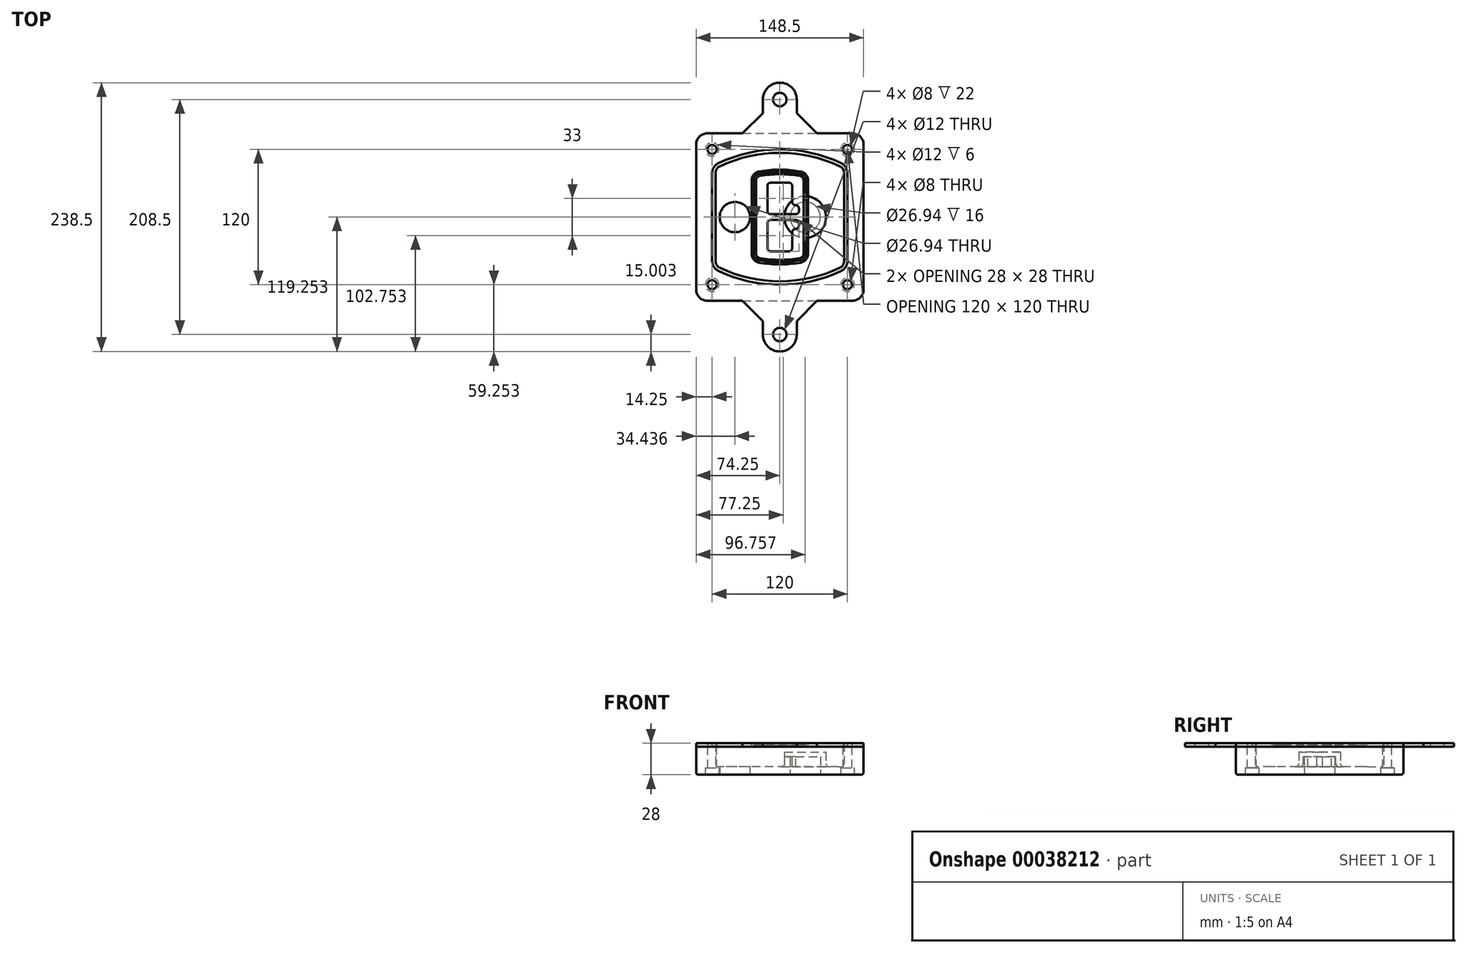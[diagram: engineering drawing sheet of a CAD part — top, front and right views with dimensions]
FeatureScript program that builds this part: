
annotation { "Feature Type Name" : "Feature", "Feature Type Description" : "" }
export const myFeature = defineFeature(function(context is Context, id is Id, definition is map)
    precondition{}
    {
        {
            var Q0;
            Q0=qCreatedBy(makeId("Top.planeOp"),FACE);
            var sketch = newSketch(context, id + "F0", { "sketchPlane" : qUnion([Q0])});
            skPoint(sketch, "E0.rect.middle", {"position": v(0, 0) * mm});
            skLineSegment(sketch, "E1.bottom", {"start": v(24.05, 28.38) * mm, "end": v(152.55, 28.38) * mm});
            skLineSegment(sketch, "E1.top", {"start": v(24.05, 176.88) * mm, "end": v(152.55, 176.88) * mm});
            skLineSegment(sketch, "E1.left", {"start": v(14.05, 38.38) * mm, "end": v(14.05, 166.88) * mm});
            skLineSegment(sketch, "E1.right", {"start": v(162.55, 38.38) * mm, "end": v(162.55, 166.88) * mm});
            skLineSegment(sketch, "E2", {"start": v(14.05, 176.88) * mm, "end": v(162.55, 28.38) * mm, "construction": true});
            skLineSegment(sketch, "E3", {"start": v(162.55, 176.88) * mm, "end": v(14.05, 28.38) * mm, "construction": true});
            skCircle(sketch, "E4", {"center": v(28.3, 162.63) * mm, "radius": 4 * mm});
            skCircle(sketch, "E5", {"center": v(148.3, 162.63) * mm, "radius": 4 * mm});
            skCircle(sketch, "E6", {"center": v(148.3, 42.63) * mm, "radius": 4 * mm});
            skCircle(sketch, "E7", {"center": v(28.3, 42.63) * mm, "radius": 4 * mm});
            skLineSegment(sketch, "E8", {"start": v(28.3, 162.63) * mm, "end": v(148.3, 162.63) * mm, "construction": true});
            skLineSegment(sketch, "E9", {"start": v(148.3, 162.63) * mm, "end": v(148.3, 42.63) * mm, "construction": true});
            skLineSegment(sketch, "E10", {"start": v(148.3, 42.63) * mm, "end": v(28.3, 42.63) * mm, "construction": true});
            skLineSegment(sketch, "E11", {"start": v(28.3, 42.63) * mm, "end": v(28.3, 162.63) * mm, "construction": true});
            skLineSegment(sketch, "E12", {"start": v(28.3, 141.46) * mm, "end": v(28.3, 63.8) * mm});
            skLineSegment(sketch, "E13", {"start": v(148.3, 141.46) * mm, "end": v(148.3, 63.8) * mm});
            skArc(sketch, "E14", {"start": v(142.56, 150.51) * mm, "mid": v(88.3, 162.63) * mm, "end": v(34.04, 150.51) * mm});
            skArc(sketch, "E15", {"start": v(34.04, 54.75) * mm, "mid": v(88.3, 42.63) * mm, "end": v(142.56, 54.75) * mm});
            skLineSegment(sketch, "E16", {"start": v(28.3, 102.63) * mm, "end": v(148.3, 102.63) * mm, "construction": true});
            skPoint(sketch, "E17.visualSharp", {"position": v(28.3, 57.63) * mm});
            skArc(sketch, "E17.filletArc", {"start": v(28.3, 63.8) * mm, "mid": v(29.86, 58.44) * mm, "end": v(34.04, 54.75) * mm});
            skPoint(sketch, "E18.visualSharp", {"position": v(28.3, 147.63) * mm});
            skArc(sketch, "E18.filletArc", {"start": v(34.04, 150.51) * mm, "mid": v(29.86, 146.82) * mm, "end": v(28.3, 141.46) * mm});
            skPoint(sketch, "E19.visualSharp", {"position": v(148.3, 147.63) * mm});
            skArc(sketch, "E19.filletArc", {"start": v(148.3, 141.46) * mm, "mid": v(146.74, 146.82) * mm, "end": v(142.56, 150.51) * mm});
            skPoint(sketch, "E20.visualSharp", {"position": v(148.3, 57.63) * mm});
            skArc(sketch, "E20.filletArc", {"start": v(142.56, 54.75) * mm, "mid": v(146.74, 58.44) * mm, "end": v(148.3, 63.8) * mm});
            skPoint(sketch, "E21.visualSharp", {"position": v(14.05, 176.88) * mm});
            skArc(sketch, "E21.filletArc", {"start": v(24.05, 176.88) * mm, "mid": v(16.98, 173.95) * mm, "end": v(14.05, 166.88) * mm});
            skPoint(sketch, "E22.visualSharp", {"position": v(162.55, 176.88) * mm});
            skArc(sketch, "E22.filletArc", {"start": v(162.55, 166.88) * mm, "mid": v(159.62, 173.95) * mm, "end": v(152.55, 176.88) * mm});
            skPoint(sketch, "E23.visualSharp", {"position": v(162.55, 28.38) * mm});
            skArc(sketch, "E23.filletArc", {"start": v(152.55, 28.38) * mm, "mid": v(159.62, 31.31) * mm, "end": v(162.55, 38.38) * mm});
            skPoint(sketch, "E24.visualSharp", {"position": v(14.05, 28.38) * mm});
            skArc(sketch, "E24.filletArc", {"start": v(14.05, 38.38) * mm, "mid": v(16.98, 31.31) * mm, "end": v(24.05, 28.38) * mm});
            skArc(sketch, "E25.0", {"start": v(145.3, 141.46) * mm, "mid": v(144.2, 145.22) * mm, "end": v(141.28, 147.8) * mm});
            skLineSegment(sketch, "E25.1", {"start": v(145.3, 141.46) * mm, "end": v(145.3, 63.8) * mm});
            skArc(sketch, "E25.2", {"start": v(141.28, 57.47) * mm, "mid": v(144.2, 60.05) * mm, "end": v(145.3, 63.8) * mm});
            skArc(sketch, "E25.3", {"start": v(35.32, 57.47) * mm, "mid": v(88.3, 45.63) * mm, "end": v(141.28, 57.47) * mm});
            skArc(sketch, "E25.4", {"start": v(31.3, 63.8) * mm, "mid": v(32.4, 60.05) * mm, "end": v(35.32, 57.47) * mm});
            skArc(sketch, "E25.5", {"start": v(141.28, 147.8) * mm, "mid": v(88.3, 159.63) * mm, "end": v(35.32, 147.8) * mm});
            skLineSegment(sketch, "E25.6", {"start": v(31.3, 141.46) * mm, "end": v(31.3, 63.8) * mm});
            skArc(sketch, "E25.7", {"start": v(35.32, 147.8) * mm, "mid": v(32.4, 145.22) * mm, "end": v(31.3, 141.46) * mm});
            skArc(sketch, "E26.0", {"start": v(32.34, 154.13) * mm, "mid": v(26.48, 148.97) * mm, "end": v(24.3, 141.46) * mm});
            skArc(sketch, "E26.1", {"start": v(144.26, 154.13) * mm, "mid": v(88.3, 166.63) * mm, "end": v(32.34, 154.13) * mm});
            skArc(sketch, "E26.2", {"start": v(152.3, 141.46) * mm, "mid": v(150.12, 148.97) * mm, "end": v(144.26, 154.13) * mm});
            skLineSegment(sketch, "E26.3", {"start": v(152.3, 141.46) * mm, "end": v(152.3, 63.8) * mm});
            skArc(sketch, "E26.4", {"start": v(144.26, 51.13) * mm, "mid": v(150.12, 56.3) * mm, "end": v(152.3, 63.8) * mm});
            skLineSegment(sketch, "E26.5", {"start": v(24.3, 141.46) * mm, "end": v(24.3, 63.8) * mm});
            skArc(sketch, "E26.6", {"start": v(32.34, 51.13) * mm, "mid": v(88.3, 38.63) * mm, "end": v(144.26, 51.13) * mm});
            skArc(sketch, "E26.7", {"start": v(24.3, 63.8) * mm, "mid": v(26.48, 56.3) * mm, "end": v(32.34, 51.13) * mm});
            skSolve(sketch);
        }
        {
            var Q0;
            Q0=makeQuery(id+"F0.imprint","IMPRINT",FACE,{"disambiguationData":[TD([[makeQuery(id+"F0.imprint","IMPRINT",EDGE,{"derivedFrom":sQuery(id+"F0.wireOp",EDGE,"E1.bottom")}),1.0]])]});
            var Q1;
            Q1=makeQuery(id+"F0.imprint","IMPRINT",FACE,{"disambiguationData":[TD([[makeQuery(id+"F0.imprint","IMPRINT",EDGE,{"derivedFrom":sQuery(id+"F0.wireOp",EDGE,"E12")}),1.0]])]});
            var Q2;
            Q2=makeQuery(id+"F0.imprint","IMPRINT",FACE,{"disambiguationData":[TD([[makeQuery(id+"F0.imprint","IMPRINT",EDGE,{"derivedFrom":sQuery(id+"F0.wireOp",EDGE,"E25.0")}),1.0]])]});
            var Q3;
            Q3=makeQuery(id+"F0.imprint","IMPRINT",FACE,{"disambiguationData":[TD([[makeQuery(id+"F0.imprint","IMPRINT",EDGE,{"derivedFrom":sQuery(id+"F0.wireOp",EDGE,"E12")}),-1.0]])]});
            extrude(context, id + "F1", {"entities" : qUnion([Q0, Q1, Q2, Q3]), "oppositeDirection" : true, "depth" : 25 * mm});
        }
        {
            var Q0;
            Q0=makeQuery(id+"F0.imprint","IMPRINT",FACE,{"disambiguationData":[TD([[makeQuery(id+"F0.imprint","IMPRINT",EDGE,{"derivedFrom":sQuery(id+"F0.wireOp",EDGE,"E12")}),1.0]])]});
            extrude(context, id + "F2", {"entities" : qUnion([Q0]), "operationType" : NewBodyOperationType.ADD, "depth" : 3 * mm});
        }
        {
            var Q0;
            Q0=makeQuery(id+"F0.imprint","IMPRINT",FACE,{"disambiguationData":[TD([[makeQuery(id+"F0.imprint","IMPRINT",EDGE,{"derivedFrom":sQuery(id+"F0.wireOp",EDGE,"E25.0")}),1.0]])]});
            extrude(context, id + "F3", {"entities" : qUnion([Q0]), "operationType" : NewBodyOperationType.REMOVE, "oppositeDirection" : true, "depth" : 18 * mm});
        }
        {
            var Q0;
            Q0=makeQuery(id+"F2.opExtrude","CAP_FACE",FACE,{"disambiguationData":[OSD([sQuery(id+"F0.wireOp",EDGE,"E12"),sQuery(id+"F0.wireOp",EDGE,"E13"),sQuery(id+"F0.wireOp",EDGE,"E14"),sQuery(id+"F0.wireOp",EDGE,"E15"),sQuery(id+"F0.wireOp",EDGE,"E17.filletArc"),sQuery(id+"F0.wireOp",EDGE,"E18.filletArc"),sQuery(id+"F0.wireOp",EDGE,"E19.filletArc"),sQuery(id+"F0.wireOp",EDGE,"E20.filletArc"),sQuery(id+"F0.wireOp",EDGE,"E25.0"),sQuery(id+"F0.wireOp",EDGE,"E25.1"),sQuery(id+"F0.wireOp",EDGE,"E25.2"),sQuery(id+"F0.wireOp",EDGE,"E25.3"),sQuery(id+"F0.wireOp",EDGE,"E25.4"),sQuery(id+"F0.wireOp",EDGE,"E25.5"),sQuery(id+"F0.wireOp",EDGE,"E25.6"),sQuery(id+"F0.wireOp",EDGE,"E25.7")])],"isStart":false});
            var sketch = newSketch(context, id + "F4", { "sketchPlane" : qUnion([Q0])});
            skArc(sketch, "E27.0", {"start": v(69.96, 62.18) * mm, "mid": v(88.3, 60.63) * mm, "end": v(106.64, 62.18) * mm});
            skArc(sketch, "E28.0", {"start": v(106.64, 143.09) * mm, "mid": v(88.3, 144.63) * mm, "end": v(69.96, 143.09) * mm});
            skLineSegment(sketch, "E29", {"start": v(63.3, 135.2) * mm, "end": v(63.3, 70.07) * mm});
            skLineSegment(sketch, "E30", {"start": v(113.3, 135.2) * mm, "end": v(113.3, 70.07) * mm});
            skLineSegment(sketch, "E31", {"start": v(63.3, 141.74) * mm, "end": v(113.3, 141.74) * mm, "construction": true});
            skLineSegment(sketch, "E32", {"start": v(63.3, 63.52) * mm, "end": v(113.3, 63.52) * mm, "construction": true});
            skPoint(sketch, "E33.visualSharp", {"position": v(63.3, 141.74) * mm});
            skArc(sketch, "E33.filletArc", {"start": v(69.96, 143.09) * mm, "mid": v(65.19, 140.36) * mm, "end": v(63.3, 135.2) * mm});
            skPoint(sketch, "E34.visualSharp", {"position": v(113.3, 141.74) * mm});
            skArc(sketch, "E34.filletArc", {"start": v(113.3, 135.2) * mm, "mid": v(111.41, 140.36) * mm, "end": v(106.64, 143.09) * mm});
            skPoint(sketch, "E35.visualSharp", {"position": v(113.3, 63.52) * mm});
            skArc(sketch, "E35.filletArc", {"start": v(106.64, 62.18) * mm, "mid": v(111.41, 64.9) * mm, "end": v(113.3, 70.07) * mm});
            skPoint(sketch, "E36.visualSharp", {"position": v(63.3, 63.52) * mm});
            skArc(sketch, "E36.filletArc", {"start": v(63.3, 70.07) * mm, "mid": v(65.19, 64.9) * mm, "end": v(69.96, 62.18) * mm});
            skArc(sketch, "E37.0", {"start": v(141.28, 147.8) * mm, "mid": v(88.3, 159.63) * mm, "end": v(35.32, 147.8) * mm});
            skArc(sketch, "E37.1", {"start": v(35.32, 147.8) * mm, "mid": v(32.4, 145.22) * mm, "end": v(31.3, 141.46) * mm});
            skLineSegment(sketch, "E37.2", {"start": v(31.3, 141.46) * mm, "end": v(31.3, 63.8) * mm});
            skArc(sketch, "E37.3", {"start": v(31.3, 63.8) * mm, "mid": v(32.4, 60.05) * mm, "end": v(35.32, 57.47) * mm});
            skArc(sketch, "E37.4", {"start": v(35.32, 57.47) * mm, "mid": v(88.3, 45.63) * mm, "end": v(141.28, 57.47) * mm});
            skArc(sketch, "E37.5", {"start": v(141.28, 57.47) * mm, "mid": v(144.2, 60.05) * mm, "end": v(145.3, 63.8) * mm});
            skLineSegment(sketch, "E37.6", {"start": v(145.3, 141.46) * mm, "end": v(145.3, 63.8) * mm});
            skArc(sketch, "E37.7", {"start": v(145.3, 141.46) * mm, "mid": v(144.2, 145.22) * mm, "end": v(141.28, 147.8) * mm});
            skLineSegment(sketch, "E38.0", {"start": v(111.3, 135.2) * mm, "end": v(111.3, 70.07) * mm});
            skArc(sketch, "E38.1", {"start": v(106.3, 64.15) * mm, "mid": v(109.88, 66.2) * mm, "end": v(111.3, 70.07) * mm});
            skArc(sketch, "E38.2", {"start": v(70.3, 64.15) * mm, "mid": v(88.3, 62.63) * mm, "end": v(106.3, 64.15) * mm});
            skArc(sketch, "E38.3", {"start": v(65.3, 70.07) * mm, "mid": v(66.72, 66.2) * mm, "end": v(70.3, 64.15) * mm});
            skLineSegment(sketch, "E38.4", {"start": v(65.3, 135.2) * mm, "end": v(65.3, 70.07) * mm});
            skArc(sketch, "E38.5", {"start": v(111.3, 135.2) * mm, "mid": v(109.88, 139.07) * mm, "end": v(106.3, 141.11) * mm});
            skArc(sketch, "E38.6", {"start": v(70.3, 141.11) * mm, "mid": v(66.72, 139.07) * mm, "end": v(65.3, 135.2) * mm});
            skArc(sketch, "E38.7", {"start": v(106.3, 141.11) * mm, "mid": v(88.3, 142.63) * mm, "end": v(70.3, 141.11) * mm});
            skArc(sketch, "E39.0", {"start": v(109.3, 135.2) * mm, "mid": v(108.36, 137.78) * mm, "end": v(105.97, 139.14) * mm});
            skLineSegment(sketch, "E39.1", {"start": v(109.3, 135.2) * mm, "end": v(109.3, 70.07) * mm});
            skArc(sketch, "E39.2", {"start": v(105.97, 66.12) * mm, "mid": v(108.36, 67.49) * mm, "end": v(109.3, 70.07) * mm});
            skArc(sketch, "E39.3", {"start": v(70.63, 66.12) * mm, "mid": v(88.3, 64.63) * mm, "end": v(105.97, 66.12) * mm});
            skArc(sketch, "E39.4", {"start": v(67.3, 70.07) * mm, "mid": v(68.24, 67.49) * mm, "end": v(70.63, 66.12) * mm});
            skArc(sketch, "E39.5", {"start": v(105.97, 139.14) * mm, "mid": v(88.3, 140.63) * mm, "end": v(70.63, 139.14) * mm});
            skLineSegment(sketch, "E39.6", {"start": v(67.3, 135.2) * mm, "end": v(67.3, 70.07) * mm});
            skArc(sketch, "E39.7", {"start": v(70.63, 139.14) * mm, "mid": v(68.24, 137.78) * mm, "end": v(67.3, 135.2) * mm});
            skLineSegment(sketch, "E40", {"start": v(63.3, 102.63) * mm, "end": v(113.3, 102.63) * mm, "construction": true});
            skLineSegment(sketch, "E41", {"start": v(77.3, 108.13) * mm, "end": v(77.3, 130.13) * mm});
            skLineSegment(sketch, "E42", {"start": v(80.3, 133.13) * mm, "end": v(96.3, 133.13) * mm});
            skLineSegment(sketch, "E43", {"start": v(99.3, 130.13) * mm, "end": v(99.3, 116.13) * mm});
            skLineSegment(sketch, "E44", {"start": v(102.3, 113.13) * mm, "end": v(102.3, 113.13) * mm});
            skLineSegment(sketch, "E45", {"start": v(105.3, 110.13) * mm, "end": v(105.3, 108.13) * mm});
            skLineSegment(sketch, "E46", {"start": v(102.3, 105.13) * mm, "end": v(80.3, 105.13) * mm});
            skPoint(sketch, "E47.visualSharp", {"position": v(77.3, 133.13) * mm});
            skArc(sketch, "E47.filletArc", {"start": v(80.3, 133.13) * mm, "mid": v(78.18, 132.25) * mm, "end": v(77.3, 130.13) * mm});
            skPoint(sketch, "E48.visualSharp", {"position": v(99.3, 133.13) * mm});
            skArc(sketch, "E48.filletArc", {"start": v(99.3, 130.13) * mm, "mid": v(98.42, 132.25) * mm, "end": v(96.3, 133.13) * mm});
            skPoint(sketch, "E49.visualSharp", {"position": v(99.3, 113.13) * mm});
            skArc(sketch, "E49.filletArc", {"start": v(99.3, 116.13) * mm, "mid": v(100.18, 114.01) * mm, "end": v(102.3, 113.13) * mm});
            skPoint(sketch, "E50.visualSharp", {"position": v(105.3, 113.13) * mm});
            skArc(sketch, "E50.filletArc", {"start": v(105.3, 110.13) * mm, "mid": v(104.42, 112.25) * mm, "end": v(102.3, 113.13) * mm});
            skPoint(sketch, "E51.visualSharp", {"position": v(105.3, 105.13) * mm});
            skArc(sketch, "E51.filletArc", {"start": v(102.3, 105.13) * mm, "mid": v(104.42, 106.01) * mm, "end": v(105.3, 108.13) * mm});
            skPoint(sketch, "E52.visualSharp", {"position": v(77.3, 105.13) * mm});
            skArc(sketch, "E52.filletArc", {"start": v(77.3, 108.13) * mm, "mid": v(78.18, 106.01) * mm, "end": v(80.3, 105.13) * mm});
            skLineSegment(sketch, "E53.0.MirrorCS", {"start": v(102.3, 100.13) * mm, "end": v(80.3, 100.13) * mm});
            skArc(sketch, "E54.0.MirrorCS", {"start": v(77.3, 97.13) * mm, "mid": v(78.18, 99.25) * mm, "end": v(80.3, 100.13) * mm});
            skLineSegment(sketch, "E55.0.MirrorCS", {"start": v(77.3, 97.13) * mm, "end": v(77.3, 75.13) * mm});
            skArc(sketch, "E56.0.MirrorCS", {"start": v(80.3, 72.13) * mm, "mid": v(78.18, 73.01) * mm, "end": v(77.3, 75.13) * mm});
            skLineSegment(sketch, "E57.0.MirrorCS", {"start": v(80.3, 72.13) * mm, "end": v(96.3, 72.13) * mm});
            skArc(sketch, "E58.0.MirrorCS", {"start": v(99.3, 75.13) * mm, "mid": v(98.42, 73.01) * mm, "end": v(96.3, 72.13) * mm});
            skLineSegment(sketch, "E59.0.MirrorCS", {"start": v(99.3, 75.13) * mm, "end": v(99.3, 89.13) * mm});
            skArc(sketch, "E60.0.MirrorCS", {"start": v(99.3, 89.13) * mm, "mid": v(100.18, 91.25) * mm, "end": v(102.3, 92.13) * mm});
            skArc(sketch, "E61.0.MirrorCS", {"start": v(105.3, 95.13) * mm, "mid": v(104.42, 93.01) * mm, "end": v(102.3, 92.13) * mm});
            skLineSegment(sketch, "E62.0.MirrorCS", {"start": v(105.3, 95.13) * mm, "end": v(105.3, 97.13) * mm});
            skArc(sketch, "E63.0.MirrorCS", {"start": v(102.3, 100.13) * mm, "mid": v(104.42, 99.25) * mm, "end": v(105.3, 97.13) * mm});
            skSolve(sketch);
        }
        {
            var Q0;
            Q0=makeQuery(id+"F4.imprint","IMPRINT",FACE,{"disambiguationData":[TD([[makeQuery(id+"F4.imprint","IMPRINT",EDGE,{"derivedFrom":sQuery(id+"F4.wireOp",EDGE,"E27.0")}),1.0]])]});
            var Q1;
            Q1=makeQuery(id+"F4.imprint","IMPRINT",FACE,{"disambiguationData":[TD([[makeQuery(id+"F4.imprint","IMPRINT",EDGE,{"derivedFrom":sQuery(id+"F4.wireOp",EDGE,"E38.0")}),-1.0]])]});
            var Q2;
            Q2=makeQuery(id+"F4.imprint","IMPRINT",FACE,{"disambiguationData":[TD([[makeQuery(id+"F4.imprint","IMPRINT",EDGE,{"derivedFrom":sQuery(id+"F4.wireOp",EDGE,"E39.0")}),1.0]])]});
            extrude(context, id + "F5", {"entities" : qUnion([Q0, Q1, Q2]), "operationType" : NewBodyOperationType.ADD, "endBound" : BoundingType.UP_TO_NEXT, "oppositeDirection" : true, "depth" : 25 * mm});
        }
        {
            var Q0;
            Q0=makeQuery(id+"F4.imprint","IMPRINT",FACE,{"disambiguationData":[TD([[makeQuery(id+"F4.imprint","IMPRINT",EDGE,{"derivedFrom":sQuery(id+"F4.wireOp",EDGE,"E38.0")}),-1.0]])]});
            extrude(context, id + "F6", {"entities" : qUnion([Q0]), "operationType" : NewBodyOperationType.REMOVE, "oppositeDirection" : true, "depth" : 2 * mm});
        }
        {
            var Q0;
            Q0=makeQuery(id+"F1.opExtrude","CAP_FACE",FACE,{"disambiguationData":[OSD([sQuery(id+"F0.wireOp",EDGE,"E1.bottom"),sQuery(id+"F0.wireOp",EDGE,"E1.top"),sQuery(id+"F0.wireOp",EDGE,"E1.left"),sQuery(id+"F0.wireOp",EDGE,"E1.right"),sQuery(id+"F0.wireOp",EDGE,"E4"),sQuery(id+"F0.wireOp",EDGE,"E5"),sQuery(id+"F0.wireOp",EDGE,"E6"),sQuery(id+"F0.wireOp",EDGE,"E7"),sQuery(id+"F0.wireOp",EDGE,"E21.filletArc"),sQuery(id+"F0.wireOp",EDGE,"E22.filletArc"),sQuery(id+"F0.wireOp",EDGE,"E23.filletArc"),sQuery(id+"F0.wireOp",EDGE,"E24.filletArc")])],"isStart":false});
            var sketch = newSketch(context, id + "F7", { "sketchPlane" : qUnion([Q0])});
            skCircle(sketch, "E64", {"center": v(110.8, -102.63) * mm, "radius": 13.47 * mm});
            skCircle(sketch, "E65", {"center": v(48.49, -102.63) * mm, "radius": 13.47 * mm});
            skLineSegment(sketch, "E66", {"start": v(162.55, -102.63) * mm, "end": v(14.05, -102.63) * mm});
            skCircle(sketch, "E67", {"center": v(110.8, -102.63) * mm, "radius": 18.47 * mm});
            skCircle(sketch, "E68", {"center": v(148.3, -162.63) * mm, "radius": 6 * mm});
            skCircle(sketch, "E69", {"center": v(28.3, -162.63) * mm, "radius": 6 * mm});
            skCircle(sketch, "E70", {"center": v(28.3, -42.63) * mm, "radius": 6 * mm});
            skCircle(sketch, "E71", {"center": v(148.3, -42.63) * mm, "radius": 6 * mm});
            skSolve(sketch);
        }
        {
            var Q0;
            {var subQ1=sQuery(id+"F7.wireOp",EDGE,"E66");var subQ4=sQuery(id+"F7.wireOp",EDGE,"E64");var subQ6=makeQuery(id+"F7.imprint","INTERSECT",VERTEX,{"disambiguationData":[OD(0.0)],"derivedFrom":[subQ4,subQ1]});Q0=makeQuery(id+"F7.imprint","IMPRINT",FACE,{"disambiguationData":[TD([[makeQuery(id+"F7.imprint","IMPRINT",EDGE,{"disambiguationData":[TD([[subQ6,-1.0]])],"derivedFrom":subQ4}),-1.0]])]});}
            var Q1;
            {var subQ0=sQuery(id+"F7.wireOp",EDGE,"E66");var subQ1=sQuery(id+"F7.wireOp",EDGE,"E64");var subQ3=makeQuery(id+"F7.imprint","INTERSECT",VERTEX,{"disambiguationData":[OD(0.0)],"derivedFrom":[subQ1,subQ0]});Q1=makeQuery(id+"F7.imprint","IMPRINT",FACE,{"disambiguationData":[TD([[makeQuery(id+"F7.imprint","IMPRINT",EDGE,{"disambiguationData":[TD([[subQ3,-1.0]])],"derivedFrom":subQ1}),1.0]])]});}
            var Q2;
            {var subQ0=sQuery(id+"F7.wireOp",EDGE,"E66");var subQ1=sQuery(id+"F7.wireOp",EDGE,"E64");var subQ3=makeQuery(id+"F7.imprint","INTERSECT",VERTEX,{"disambiguationData":[OD(0.0)],"derivedFrom":[subQ1,subQ0]});Q2=makeQuery(id+"F7.imprint","IMPRINT",FACE,{"disambiguationData":[TD([[makeQuery(id+"F7.imprint","IMPRINT",EDGE,{"disambiguationData":[TD([[subQ3,1.0]])],"derivedFrom":subQ1}),1.0]])]});}
            var Q3;
            {var subQ1=sQuery(id+"F7.wireOp",EDGE,"E66");var subQ4=sQuery(id+"F7.wireOp",EDGE,"E64");var subQ6=makeQuery(id+"F7.imprint","INTERSECT",VERTEX,{"disambiguationData":[OD(0.0)],"derivedFrom":[subQ4,subQ1]});Q3=makeQuery(id+"F7.imprint","IMPRINT",FACE,{"disambiguationData":[TD([[makeQuery(id+"F7.imprint","IMPRINT",EDGE,{"disambiguationData":[TD([[subQ6,1.0]])],"derivedFrom":subQ4}),-1.0]])]});}
            extrude(context, id + "F8", {"entities" : qUnion([Q0, Q1, Q2, Q3]), "operationType" : NewBodyOperationType.ADD, "oppositeDirection" : true, "depth" : 20 * mm});
        }
        {
            var Q0;
            {var subQ0=sQuery(id+"F7.wireOp",EDGE,"E66");var subQ1=sQuery(id+"F7.wireOp",EDGE,"E64");var subQ3=makeQuery(id+"F7.imprint","INTERSECT",VERTEX,{"disambiguationData":[OD(0.0)],"derivedFrom":[subQ1,subQ0]});Q0=makeQuery(id+"F7.imprint","IMPRINT",FACE,{"disambiguationData":[TD([[makeQuery(id+"F7.imprint","IMPRINT",EDGE,{"disambiguationData":[TD([[subQ3,-1.0]])],"derivedFrom":subQ1}),1.0]])]});}
            var Q1;
            {var subQ0=sQuery(id+"F7.wireOp",EDGE,"E66");var subQ1=sQuery(id+"F7.wireOp",EDGE,"E64");var subQ3=makeQuery(id+"F7.imprint","INTERSECT",VERTEX,{"disambiguationData":[OD(0.0)],"derivedFrom":[subQ1,subQ0]});Q1=makeQuery(id+"F7.imprint","IMPRINT",FACE,{"disambiguationData":[TD([[makeQuery(id+"F7.imprint","IMPRINT",EDGE,{"disambiguationData":[TD([[subQ3,1.0]])],"derivedFrom":subQ1}),1.0]])]});}
            extrude(context, id + "F9", {"entities" : qUnion([Q0, Q1]), "operationType" : NewBodyOperationType.REMOVE, "oppositeDirection" : true, "depth" : 16 * mm});
        }
        {
            var Q0;
            {var subQ0=sQuery(id+"F7.wireOp",EDGE,"E66");var subQ1=sQuery(id+"F7.wireOp",EDGE,"E65");var subQ3=makeQuery(id+"F7.imprint","INTERSECT",VERTEX,{"disambiguationData":[OD(0.0)],"derivedFrom":[subQ1,subQ0]});Q0=makeQuery(id+"F7.imprint","IMPRINT",FACE,{"disambiguationData":[TD([[makeQuery(id+"F7.imprint","IMPRINT",EDGE,{"disambiguationData":[TD([[subQ3,-1.0]])],"derivedFrom":subQ1}),1.0]])]});}
            var Q1;
            {var subQ0=sQuery(id+"F7.wireOp",EDGE,"E66");var subQ1=sQuery(id+"F7.wireOp",EDGE,"E65");var subQ3=makeQuery(id+"F7.imprint","INTERSECT",VERTEX,{"disambiguationData":[OD(0.0)],"derivedFrom":[subQ1,subQ0]});Q1=makeQuery(id+"F7.imprint","IMPRINT",FACE,{"disambiguationData":[TD([[makeQuery(id+"F7.imprint","IMPRINT",EDGE,{"disambiguationData":[TD([[subQ3,1.0]])],"derivedFrom":subQ1}),1.0]])]});}
            extrude(context, id + "F10", {"entities" : qUnion([Q0, Q1]), "operationType" : NewBodyOperationType.REMOVE, "oppositeDirection" : true, "depth" : 25 * mm});
        }
        {
            var Q0;
            Q0=makeQuery(id+"F7.imprint","IMPRINT",FACE,{"disambiguationData":[TD([[makeQuery(id+"F7.imprint","IMPRINT",EDGE,{"derivedFrom":sQuery(id+"F7.wireOp",EDGE,"E68")}),1.0]])]});
            var Q1;
            Q1=makeQuery(id+"F7.imprint","IMPRINT",FACE,{"disambiguationData":[TD([[makeQuery(id+"F7.imprint","IMPRINT",EDGE,{"derivedFrom":makeQuery(id+"F1.opExtrude","CAP_EDGE",EDGE,{"disambiguationData":[OSD([sQuery(id+"F0.wireOp",EDGE,"E5")])],"isStart":false})}),-1.0]])]});
            var Q2;
            Q2=makeQuery(id+"F7.imprint","IMPRINT",FACE,{"disambiguationData":[TD([[makeQuery(id+"F7.imprint","IMPRINT",EDGE,{"derivedFrom":sQuery(id+"F7.wireOp",EDGE,"E69")}),1.0]])]});
            var Q3;
            Q3=makeQuery(id+"F7.imprint","IMPRINT",FACE,{"disambiguationData":[TD([[makeQuery(id+"F7.imprint","IMPRINT",EDGE,{"derivedFrom":makeQuery(id+"F1.opExtrude","CAP_EDGE",EDGE,{"disambiguationData":[OSD([sQuery(id+"F0.wireOp",EDGE,"E4")])],"isStart":false})}),-1.0]])]});
            var Q4;
            Q4=makeQuery(id+"F7.imprint","IMPRINT",FACE,{"disambiguationData":[TD([[makeQuery(id+"F7.imprint","IMPRINT",EDGE,{"derivedFrom":sQuery(id+"F7.wireOp",EDGE,"E70")}),1.0]])]});
            var Q5;
            Q5=makeQuery(id+"F7.imprint","IMPRINT",FACE,{"disambiguationData":[TD([[makeQuery(id+"F7.imprint","IMPRINT",EDGE,{"derivedFrom":makeQuery(id+"F1.opExtrude","CAP_EDGE",EDGE,{"disambiguationData":[OSD([sQuery(id+"F0.wireOp",EDGE,"E7")])],"isStart":false})}),-1.0]])]});
            var Q6;
            Q6=makeQuery(id+"F7.imprint","IMPRINT",FACE,{"disambiguationData":[TD([[makeQuery(id+"F7.imprint","IMPRINT",EDGE,{"derivedFrom":sQuery(id+"F7.wireOp",EDGE,"E71")}),1.0]])]});
            var Q7;
            Q7=makeQuery(id+"F7.imprint","IMPRINT",FACE,{"disambiguationData":[TD([[makeQuery(id+"F7.imprint","IMPRINT",EDGE,{"derivedFrom":makeQuery(id+"F1.opExtrude","CAP_EDGE",EDGE,{"disambiguationData":[OSD([sQuery(id+"F0.wireOp",EDGE,"E6")])],"isStart":false})}),-1.0]])]});
            extrude(context, id + "F11", {"entities" : qUnion([Q0, Q1, Q2, Q3, Q4, Q5, Q6, Q7]), "operationType" : NewBodyOperationType.REMOVE, "oppositeDirection" : true, "depth" : 6 * mm});
        }
        {
            var Q0;
            Q0=makeQuery(id+"F9.boolean.opBoolean","COPY",FACE,{"derivedFrom":makeQuery(id+"F9.opExtrude","CAP_FACE",FACE,{"disambiguationData":[OSD([sQuery(id+"F7.wireOp",EDGE,"E64")])],"isStart":false})});
            var sketch = newSketch(context, id + "F12", { "sketchPlane" : qUnion([Q0])});
            skArc(sketch, "E72.0", {"start": v(99.3, -88.19) * mm, "mid": v(94.75, -93.5) * mm, "end": v(92.5, -100.13) * mm});
            skArc(sketch, "E72.1", {"start": v(92.5, -105.13) * mm, "mid": v(94.75, -111.76) * mm, "end": v(99.3, -117.08) * mm});
            skLineSegment(sketch, "E73", {"start": v(92.5, -105.13) * mm, "end": v(102.3, -105.13) * mm});
            skLineSegment(sketch, "E74.0", {"start": v(102.3, -100.13) * mm, "end": v(92.5, -100.13) * mm});
            skArc(sketch, "E74.1", {"start": v(102.3, -100.13) * mm, "mid": v(104.42, -99.25) * mm, "end": v(105.3, -97.13) * mm});
            skLineSegment(sketch, "E74.2", {"start": v(105.3, -95.13) * mm, "end": v(105.3, -97.13) * mm});
            skArc(sketch, "E74.3", {"start": v(105.3, -95.13) * mm, "mid": v(104.42, -93.01) * mm, "end": v(102.3, -92.13) * mm});
            skArc(sketch, "E74.4", {"start": v(99.3, -89.13) * mm, "mid": v(100.18, -91.25) * mm, "end": v(102.3, -92.13) * mm});
            skLineSegment(sketch, "E74.5", {"start": v(99.3, -88.19) * mm, "end": v(99.3, -89.13) * mm});
            skLineSegment(sketch, "E74.7", {"start": v(102.3, -105.13) * mm, "end": v(92.5, -105.13) * mm});
            skArc(sketch, "E74.8", {"start": v(102.3, -105.13) * mm, "mid": v(104.42, -106.01) * mm, "end": v(105.3, -108.13) * mm});
            skLineSegment(sketch, "E74.9", {"start": v(105.3, -110.13) * mm, "end": v(105.3, -108.13) * mm});
            skArc(sketch, "E74.10", {"start": v(105.3, -110.13) * mm, "mid": v(104.42, -112.25) * mm, "end": v(102.3, -113.13) * mm});
            skArc(sketch, "E74.11", {"start": v(99.3, -116.13) * mm, "mid": v(100.18, -114.01) * mm, "end": v(102.3, -113.13) * mm});
            skLineSegment(sketch, "E74.12", {"start": v(99.3, -117.08) * mm, "end": v(99.3, -116.13) * mm});
            skPoint(sketch, "E75.orphan", {"position": v(99.3, -130.13) * mm});
            skPoint(sketch, "E76.orphan", {"position": v(80.3, -105.13) * mm});
            skPoint(sketch, "E77.orphan", {"position": v(80.3, -100.13) * mm});
            skPoint(sketch, "E78.orphan", {"position": v(99.3, -75.13) * mm});
            skSolve(sketch);
        }
        {
            var Q0;
            {var subQ7=sQuery(id+"F12.wireOp",EDGE,"E72.0");var subQ14=sQuery(id+"F12.wireOp",EDGE,"E72.1");var subQ16=sQuery(id+"F12.wireOp",EDGE,"E74.1");var subQ18=sQuery(id+"F12.wireOp",EDGE,"E74.8");Q0=qUnion([makeQuery(id+"F12.imprint","IMPRINT",FACE,{"disambiguationData":[TD([[makeQuery(id+"F12.imprint","IMPRINT",EDGE,{"derivedFrom":subQ7}),1.0]])]}),makeQuery(id+"F12.imprint","IMPRINT",FACE,{"disambiguationData":[TD([[makeQuery(id+"F12.imprint","IMPRINT",EDGE,{"derivedFrom":subQ14}),1.0]])]}),makeQuery(id+"F12.imprint","IMPRINT",FACE,{"disambiguationData":[TD([[makeQuery(id+"F12.imprint","IMPRINT",EDGE,{"derivedFrom":subQ16}),1.0]])]}),makeQuery(id+"F12.imprint","IMPRINT",FACE,{"disambiguationData":[TD([[makeQuery(id+"F12.imprint","IMPRINT",EDGE,{"derivedFrom":subQ18}),-1.0]])]})]);}
            var Q1;
            Q1=makeQuery(id+"F5.boolean.opBoolean","SPLIT",FACE,{"disambiguationData":[TD([makeQuery(id+"F5.opExtrude","SWEPT_FACE",FACE,{"disambiguationData":[OSD([sQuery(id+"F4.wireOp",EDGE,"E41")])]})])],"derivedFrom":makeQuery(id+"F3.boolean.opBoolean","COPY",FACE,{"derivedFrom":makeQuery(id+"F3.opExtrude","CAP_FACE",FACE,{"disambiguationData":[OSD([sQuery(id+"F0.wireOp",EDGE,"E25.0"),sQuery(id+"F0.wireOp",EDGE,"E25.1"),sQuery(id+"F0.wireOp",EDGE,"E25.2"),sQuery(id+"F0.wireOp",EDGE,"E25.3"),sQuery(id+"F0.wireOp",EDGE,"E25.4"),sQuery(id+"F0.wireOp",EDGE,"E25.5"),sQuery(id+"F0.wireOp",EDGE,"E25.6"),sQuery(id+"F0.wireOp",EDGE,"E25.7")])],"isStart":false})})});
            extrude(context, id + "F13", {"entities" : qUnion([Q0]), "operationType" : NewBodyOperationType.REMOVE, "endBound" : BoundingType.UP_TO_SURFACE, "endBoundEntityFace" : qUnion([Q1]), "depth" : 25 * mm});
        }
        {
            var Q0;
            Q0=makeQuery(id+"F3.boolean.opBoolean","COPY",EDGE,{"derivedFrom":makeQuery(id+"F3.opExtrude","CAP_EDGE",EDGE,{"disambiguationData":[OSD([sQuery(id+"F0.wireOp",EDGE,"E25.6")])],"isStart":false})});
            var Q1;
            Q1=makeQuery(id+"F8.boolean.opBoolean","INTERSECT",EDGE,{"derivedFrom":[makeQuery(id+"F5.opExtrude","SWEPT_FACE",FACE,{"disambiguationData":[OSD([sQuery(id+"F4.wireOp",EDGE,"E30")])]}),makeQuery(id+"F8.opExtrude","CAP_FACE",FACE,{"disambiguationData":[OSD([sQuery(id+"F7.wireOp",EDGE,"E67")])],"isStart":false})]});
            var Q2;
            Q2=makeQuery(id+"F8.boolean.opBoolean","INTERSECT",EDGE,{"disambiguationData":[OD(1.0)],"derivedFrom":[makeQuery(id+"F5.opExtrude","SWEPT_FACE",FACE,{"disambiguationData":[OSD([sQuery(id+"F4.wireOp",EDGE,"E30")])]}),makeQuery(id+"F8.opExtrude","SWEPT_FACE",FACE,{"disambiguationData":[OSD([sQuery(id+"F7.wireOp",EDGE,"E67")])]})]});
            var Q3;
            {var subQ0=sQuery(id+"F4.wireOp",EDGE,"E30");Q3=makeQuery(id+"F8.boolean.opBoolean","SPLIT",EDGE,{"disambiguationData":[TD([makeQuery(id+"F5.opExtrude","SWEPT_FACE",FACE,{"disambiguationData":[OSD([sQuery(id+"F4.wireOp",EDGE,"E35.filletArc")])]})])],"derivedFrom":makeQuery(id+"F5.opExtrude","CAP_EDGE",EDGE,{"disambiguationData":[OSD([subQ0])],"isStart":false})});}
            var Q4;
            {var subQ0=sQuery(id+"F0.wireOp",EDGE,"E25.7");var subQ1=sQuery(id+"F0.wireOp",EDGE,"E25.1");var subQ2=sQuery(id+"F0.wireOp",EDGE,"E25.6");var subQ3=sQuery(id+"F0.wireOp",EDGE,"E25.5");var subQ4=sQuery(id+"F0.wireOp",EDGE,"E25.4");var subQ5=sQuery(id+"F0.wireOp",EDGE,"E25.0");var subQ6=sQuery(id+"F0.wireOp",EDGE,"E25.2");var subQ7=sQuery(id+"F0.wireOp",EDGE,"E25.3");Q4=makeQuery(id+"F8.boolean.opBoolean","INTERSECT",EDGE,{"derivedFrom":[makeQuery(id+"F5.boolean.opBoolean","SPLIT",FACE,{"disambiguationData":[TD([makeQuery(id+"F2.opExtrude","SWEPT_FACE",FACE,{"disambiguationData":[OSD([subQ5])]})])],"derivedFrom":makeQuery(id+"F3.boolean.opBoolean","COPY",FACE,{"derivedFrom":makeQuery(id+"F3.opExtrude","CAP_FACE",FACE,{"disambiguationData":[OSD([subQ5,subQ1,subQ6,subQ7,subQ4,subQ3,subQ2,subQ0])],"isStart":false})})}),makeQuery(id+"F8.opExtrude","SWEPT_FACE",FACE,{"disambiguationData":[OSD([sQuery(id+"F7.wireOp",EDGE,"E67")])]})]});}
            var Q5;
            Q5=makeQuery(id+"F8.boolean.opBoolean","INTERSECT",EDGE,{"disambiguationData":[OD(0.0)],"derivedFrom":[makeQuery(id+"F5.opExtrude","SWEPT_FACE",FACE,{"disambiguationData":[OSD([sQuery(id+"F4.wireOp",EDGE,"E30")])]}),makeQuery(id+"F8.opExtrude","SWEPT_FACE",FACE,{"disambiguationData":[OSD([sQuery(id+"F7.wireOp",EDGE,"E67")])]})]});
            fillet(context, id + "F14", {"entities" : qUnion([Q0, Q1, Q2, Q3, Q4, Q5]), "radius" : 3 * mm, "tangentPropagation" : true, "allowEdgeOverflow" : false});
        }
        {
            var Q0;
            Q0=makeQuery(id+"F1.opExtrude","CAP_EDGE",EDGE,{"disambiguationData":[OSD([sQuery(id+"F0.wireOp",EDGE,"E1.bottom")])],"isStart":false});
            fillet(context, id + "F15", {"entities" : qUnion([Q0]), "radius" : 2 * mm, "tangentPropagation" : true, "allowEdgeOverflow" : false});
        }
        {
            var Q0;
            Q0=qCreatedBy(makeId("Top.planeOp"),FACE);
            var sketch = newSketch(context, id + "F16", { "sketchPlane" : qUnion([Q0])});
            skLineSegment(sketch, "E79", {"start": v(73.3, 194.88) * mm, "end": v(73.3, 206.88) * mm});
            skLineSegment(sketch, "E80", {"start": v(88.3, 176.88) * mm, "end": v(88.3, 206.88) * mm, "construction": true});
            skCircle(sketch, "E81", {"center": v(88.3, 206.88) * mm, "radius": 6 * mm});
            skArc(sketch, "E82", {"start": v(103.3, 206.88) * mm, "mid": v(88.3, 221.88) * mm, "end": v(73.3, 206.88) * mm});
            skLineSegment(sketch, "E83", {"start": v(73.3, 194.88) * mm, "end": v(55.3, 176.88) * mm});
            skLineSegment(sketch, "E84", {"start": v(103.3, 194.88) * mm, "end": v(121.3, 176.88) * mm});
            skLineSegment(sketch, "E85", {"start": v(103.3, 206.88) * mm, "end": v(103.3, 194.88) * mm});
            skLineSegment(sketch, "E86.0", {"start": v(14.05, 38.38) * mm, "end": v(14.05, 166.88) * mm});
            skLineSegment(sketch, "E86.1", {"start": v(162.55, 38.38) * mm, "end": v(162.55, 166.88) * mm});
            skLineSegment(sketch, "E86.2", {"start": v(24.05, 176.88) * mm, "end": v(152.55, 176.88) * mm});
            skLineSegment(sketch, "E86.3", {"start": v(24.05, 28.38) * mm, "end": v(152.55, 28.38) * mm});
            skLineSegment(sketch, "E87", {"start": v(14.05, 102.63) * mm, "end": v(162.55, 102.63) * mm, "construction": true});
            skLineSegment(sketch, "E88.MirrorCS", {"start": v(24.05, 28.38) * mm, "end": v(152.55, 28.38) * mm, "construction": true});
            skArc(sketch, "E89.MirrorCS", {"start": v(103.3, -1.62) * mm, "mid": v(88.3, -16.62) * mm, "end": v(73.3, -1.62) * mm});
            skLineSegment(sketch, "E90.MirrorCS", {"start": v(73.3, 10.38) * mm, "end": v(55.3, 28.38) * mm});
            skLineSegment(sketch, "E91.MirrorCS", {"start": v(103.3, -1.62) * mm, "end": v(103.3, 10.38) * mm});
            skCircle(sketch, "E92.MirrorC", {"center": v(88.3, -1.62) * mm, "radius": 6 * mm, "construction": true});
            skLineSegment(sketch, "E93.MirrorCS", {"start": v(103.3, 10.38) * mm, "end": v(121.3, 28.38) * mm});
            skLineSegment(sketch, "E94.MirrorCS", {"start": v(88.3, 28.38) * mm, "end": v(88.3, -1.62) * mm, "construction": true});
            skLineSegment(sketch, "E95.MirrorCS", {"start": v(73.3, 10.38) * mm, "end": v(73.3, -1.62) * mm});
            skArc(sketch, "E96.0", {"start": v(24.05, 176.88) * mm, "mid": v(16.98, 173.95) * mm, "end": v(14.05, 166.88) * mm});
            skArc(sketch, "E96.1", {"start": v(162.55, 166.88) * mm, "mid": v(159.62, 173.95) * mm, "end": v(152.55, 176.88) * mm});
            skCircle(sketch, "E96.2", {"center": v(148.3, 162.63) * mm, "radius": 4 * mm});
            skCircle(sketch, "E96.3", {"center": v(28.3, 162.63) * mm, "radius": 4 * mm});
            skCircle(sketch, "E96.4", {"center": v(28.3, 42.63) * mm, "radius": 4 * mm});
            skArc(sketch, "E96.5", {"start": v(14.05, 38.38) * mm, "mid": v(16.98, 31.31) * mm, "end": v(24.05, 28.38) * mm});
            skArc(sketch, "E96.6", {"start": v(152.55, 28.38) * mm, "mid": v(159.62, 31.31) * mm, "end": v(162.55, 38.38) * mm});
            skCircle(sketch, "E96.7", {"center": v(148.3, 42.63) * mm, "radius": 4 * mm});
            skArc(sketch, "E96.8", {"start": v(142.56, 54.75) * mm, "mid": v(146.74, 58.44) * mm, "end": v(148.3, 63.8) * mm});
            skLineSegment(sketch, "E96.9", {"start": v(148.3, 141.46) * mm, "end": v(148.3, 63.8) * mm});
            skArc(sketch, "E96.10", {"start": v(148.3, 141.46) * mm, "mid": v(146.74, 146.82) * mm, "end": v(142.56, 150.51) * mm});
            skArc(sketch, "E96.11", {"start": v(142.56, 150.51) * mm, "mid": v(88.3, 162.63) * mm, "end": v(34.04, 150.51) * mm});
            skPoint(sketch, "E96.12", {"position": v(34.04, 150.51) * mm});
            skArc(sketch, "E96.13", {"start": v(34.04, 150.51) * mm, "mid": v(29.86, 146.82) * mm, "end": v(28.3, 141.46) * mm});
            skLineSegment(sketch, "E96.14", {"start": v(28.3, 141.46) * mm, "end": v(28.3, 63.8) * mm});
            skArc(sketch, "E96.15", {"start": v(28.3, 63.8) * mm, "mid": v(29.86, 58.44) * mm, "end": v(34.04, 54.75) * mm});
            skArc(sketch, "E96.16", {"start": v(34.04, 54.75) * mm, "mid": v(88.3, 42.63) * mm, "end": v(142.56, 54.75) * mm});
            skSolve(sketch);
        }
        {
            var Q0;
            Q0 = qSketchRegion(id + "F16", true);
            var Q1;
            Q1=makeQuery(id+"F2.opExtrude","CAP_FACE",FACE,{"disambiguationData":[OSD([sQuery(id+"F0.wireOp",EDGE,"E12"),sQuery(id+"F0.wireOp",EDGE,"E13"),sQuery(id+"F0.wireOp",EDGE,"E14"),sQuery(id+"F0.wireOp",EDGE,"E15"),sQuery(id+"F0.wireOp",EDGE,"E17.filletArc"),sQuery(id+"F0.wireOp",EDGE,"E18.filletArc"),sQuery(id+"F0.wireOp",EDGE,"E19.filletArc"),sQuery(id+"F0.wireOp",EDGE,"E20.filletArc"),sQuery(id+"F0.wireOp",EDGE,"E25.0"),sQuery(id+"F0.wireOp",EDGE,"E25.1"),sQuery(id+"F0.wireOp",EDGE,"E25.2"),sQuery(id+"F0.wireOp",EDGE,"E25.3"),sQuery(id+"F0.wireOp",EDGE,"E25.4"),sQuery(id+"F0.wireOp",EDGE,"E25.5"),sQuery(id+"F0.wireOp",EDGE,"E25.6"),sQuery(id+"F0.wireOp",EDGE,"E25.7")])],"isStart":false});
            extrude(context, id + "F17", {"entities" : qUnion([Q0]), "endBound" : BoundingType.UP_TO_SURFACE, "endBoundEntityFace" : qUnion([Q1]), "depth" : 25 * mm});
        }
        {
            var Q0;
            Q0=makeQuery(id+"F17.opExtrude","CAP_FACE",FACE,{"disambiguationData":[OSD([sQuery(id+"F16.wireOp",EDGE,"E79"),sQuery(id+"F16.wireOp",EDGE,"E81"),sQuery(id+"F16.wireOp",EDGE,"E82"),sQuery(id+"F16.wireOp",EDGE,"E83"),sQuery(id+"F16.wireOp",EDGE,"E84"),sQuery(id+"F16.wireOp",EDGE,"E85"),sQuery(id+"F16.wireOp",EDGE,"E86.0"),sQuery(id+"F16.wireOp",EDGE,"E86.1"),sQuery(id+"F16.wireOp",EDGE,"E86.2"),sQuery(id+"F16.wireOp",EDGE,"E86.3"),sQuery(id+"F16.wireOp",EDGE,"E89.MirrorCS"),sQuery(id+"F16.wireOp",EDGE,"E90.MirrorCS"),sQuery(id+"F16.wireOp",EDGE,"E91.MirrorCS"),sQuery(id+"F16.wireOp",EDGE,"E93.MirrorCS"),sQuery(id+"F16.wireOp",EDGE,"E95.MirrorCS"),sQuery(id+"F16.wireOp",EDGE,"E96.0"),sQuery(id+"F16.wireOp",EDGE,"E96.1"),sQuery(id+"F16.wireOp",EDGE,"E96.2"),sQuery(id+"F16.wireOp",EDGE,"E96.3"),sQuery(id+"F16.wireOp",EDGE,"E96.4"),sQuery(id+"F16.wireOp",EDGE,"E96.5"),sQuery(id+"F16.wireOp",EDGE,"E96.6"),sQuery(id+"F16.wireOp",EDGE,"E96.7"),sQuery(id+"F16.wireOp",EDGE,"E96.8"),sQuery(id+"F16.wireOp",EDGE,"E96.9"),sQuery(id+"F16.wireOp",EDGE,"E96.10"),sQuery(id+"F16.wireOp",EDGE,"E96.11"),sQuery(id+"F16.wireOp",EDGE,"E96.13"),sQuery(id+"F16.wireOp",EDGE,"E96.14"),sQuery(id+"F16.wireOp",EDGE,"E96.15"),sQuery(id+"F16.wireOp",EDGE,"E96.16")])],"isStart":false});
            var sketch = newSketch(context, id + "F18", { "sketchPlane" : qUnion([Q0])});
            skCircle(sketch, "E97", {"center": v(88.3, -1.62) * mm, "radius": 6 * mm});
            skSolve(sketch);
        }
        {
            var Q0;
            Q0=makeQuery(id+"F18.imprint","IMPRINT",FACE,{"disambiguationData":[TD([[makeQuery(id+"F18.imprint","IMPRINT",EDGE,{"derivedFrom":sQuery(id+"F18.wireOp",EDGE,"E97")}),1.0]])]});
            extrude(context, id + "F19", {"entities" : qUnion([Q0]), "operationType" : NewBodyOperationType.REMOVE, "endBound" : BoundingType.THROUGH_ALL, "oppositeDirection" : true, "depth" : 25 * mm});
        }
    });
